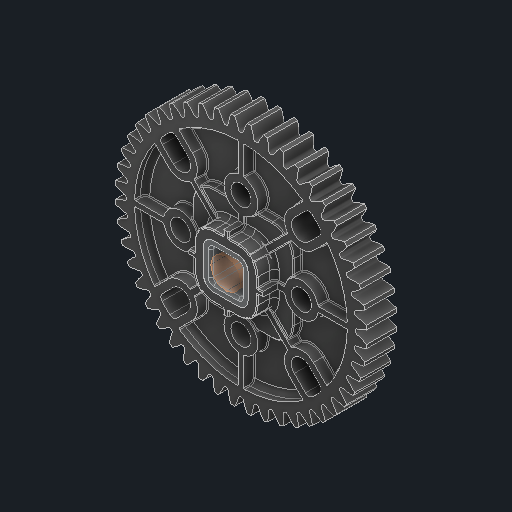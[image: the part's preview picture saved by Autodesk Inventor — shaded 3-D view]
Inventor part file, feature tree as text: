
AUTODESK INVENTOR PART (.ipt)
format: ipt  version: 2025 (Build 290162000, 162)  size: 2,941,952 bytes
history: native  units: in
note: dims shown in document units (in); Inventor stores cm internally (conversion verified against a paired STEP export)
features: other x3, extrude x3, sketch x2
ambient origin geometry x8: Origin, YZ Plane, XZ Plane, XY Plane, X Axis, Y Axis, Z Axis, Center Point
bodies: Solid1 (feature_tree), Solid2 (feature_tree)
feature tree (8):
  other  "276-7573-001_OVERMOLD Rev7_48T 24DP Gear_1:1"
  extrude  "Extrusion1"  Depth=0.3937in TaperAngle=0.0deg
  extrude  "Extrusion2"  Depth=0.125in TaperAngle=0.0deg
  other  "Srf1"
  sketch  "Sketch2"  dims[d0=0.25in d1=0.3937in d2=0.0in]
  sketch  "Sketch3"  dims[d3=0.125in d4=0.0in d5=0.125in d6=0.0in]
  other  "276-7573-002 Rev7_2:1"
  extrude  "ExtrusionSrf1"  [1 undecoded]
note: 1 required parameter value undecoded (feature->parameter linkage not recoverable at this tier; creation-order binding heuristic only, values carry confidence <= 0.55)
